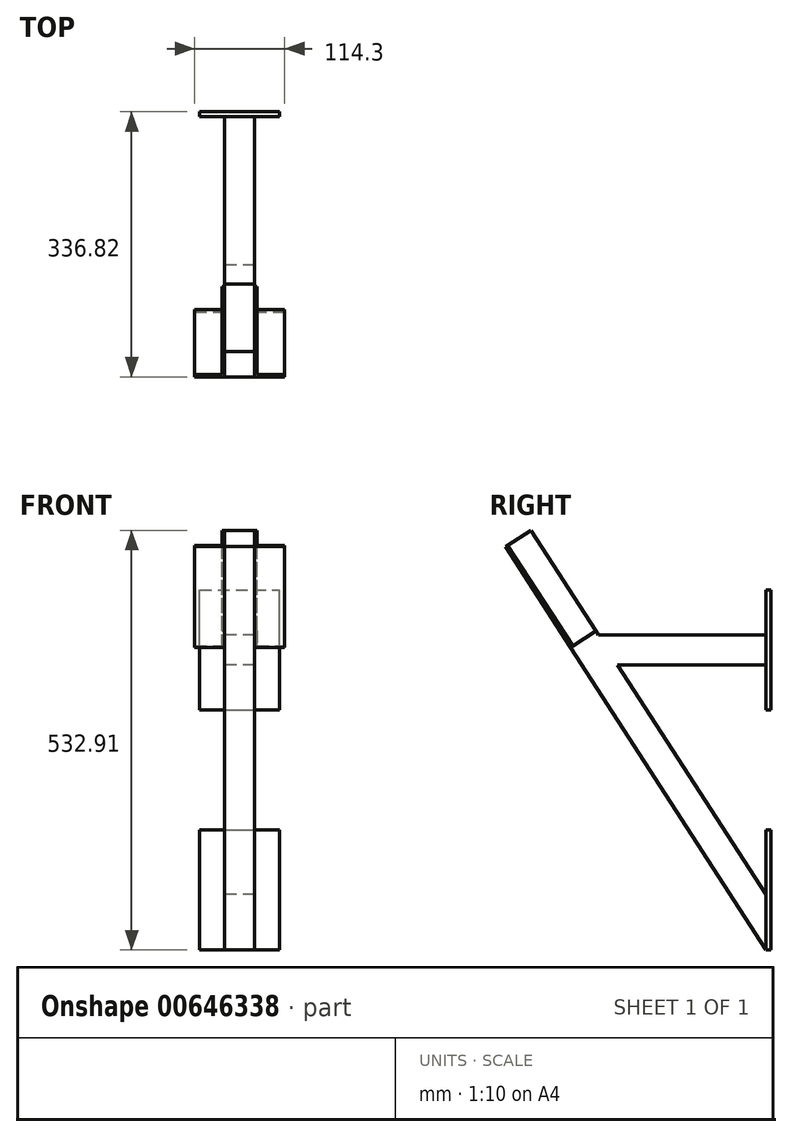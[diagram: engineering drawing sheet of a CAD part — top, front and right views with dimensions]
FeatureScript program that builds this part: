
annotation { "Feature Type Name" : "Feature", "Feature Type Description" : "" }
export const myFeature = defineFeature(function(context is Context, id is Id, definition is map)
    precondition{}
    {
        {
            var Q0;
            Q0=qCreatedBy(makeId("Front.planeOp"),FACE);
            var sketch = newSketch(context, id + "F0", { "sketchPlane" : qUnion([Q0])});
            skLineSegment(sketch, "E0.bottom", {"start": v(-50.8, 0) * mm, "end": v(50.8, 0) * mm});
            skLineSegment(sketch, "E0.top", {"start": v(-50.8, 152.4) * mm, "end": v(50.8, 152.4) * mm});
            skLineSegment(sketch, "E0.left", {"start": v(-50.8, 0) * mm, "end": v(-50.8, 152.4) * mm});
            skLineSegment(sketch, "E0.right", {"start": v(50.8, 0) * mm, "end": v(50.8, 152.4) * mm});
            skLineSegment(sketch, "E1.bottom", {"start": v(-50.8, 304.8) * mm, "end": v(50.8, 304.8) * mm});
            skLineSegment(sketch, "E1.top", {"start": v(-50.8, 457.2) * mm, "end": v(50.8, 457.2) * mm});
            skLineSegment(sketch, "E1.left", {"start": v(-50.8, 304.8) * mm, "end": v(-50.8, 457.2) * mm});
            skLineSegment(sketch, "E1.right", {"start": v(50.8, 304.8) * mm, "end": v(50.8, 457.2) * mm});
            skSolve(sketch);
        }
        {
            var Q0;
            Q0=makeQuery(id+"F0.imprint","IMPRINT",FACE,{"disambiguationData":[TD([[makeQuery(id+"F0.imprint","IMPRINT",EDGE,{"derivedFrom":sQuery(id+"F0.wireOp",EDGE,"E1.bottom")}),1.0]])]});
            var Q1;
            Q1=makeQuery(id+"F0.imprint","IMPRINT",FACE,{"disambiguationData":[TD([[makeQuery(id+"F0.imprint","IMPRINT",EDGE,{"derivedFrom":sQuery(id+"F0.wireOp",EDGE,"E0.bottom")}),1.0]])]});
            extrude(context, id + "F1", {"entities" : qUnion([Q0, Q1]), "oppositeDirection" : true, "depth" : 6.35 * mm, "offsetDistance" : 25.4 * mm});
        }
        {
            var Q0;
            Q0=qCreatedBy(makeId("Right.planeOp"),FACE);
            var sketch = newSketch(context, id + "F2", { "sketchPlane" : qUnion([Q0])});
            skLineSegment(sketch, "E2.0.0", {"start": v(0, 0) * mm, "end": v(0, 152.4) * mm});
            skLineSegment(sketch, "E2.0.1", {"start": v(0, 152.4) * mm, "end": v(6.35, 152.4) * mm});
            skLineSegment(sketch, "E2.0.2", {"start": v(6.35, 152.4) * mm, "end": v(6.35, 0) * mm});
            skLineSegment(sketch, "E2.0.3", {"start": v(6.35, 0) * mm, "end": v(0, 0) * mm});
            skLineSegment(sketch, "E3.0", {"start": v(0, 304.8) * mm, "end": v(0, 457.2) * mm});
            skLineSegment(sketch, "E4.0", {"start": v(6.35, 304.8) * mm, "end": v(0, 304.8) * mm});
            skLineSegment(sketch, "E5", {"start": v(0, 0) * mm, "end": v(-330.47, 512.25) * mm});
            skLineSegment(sketch, "E6.0", {"start": v(0, 70.28) * mm, "end": v(-298.45, 532.9) * mm});
            skLineSegment(sketch, "E7", {"start": v(-330.47, 512.25) * mm, "end": v(-298.45, 532.9) * mm});
            skLineSegment(sketch, "E8", {"start": v(0, 381) * mm, "end": v(-200.45, 381) * mm});
            skLineSegment(sketch, "E9.0", {"start": v(0, 400.05) * mm, "end": v(-212.74, 400.05) * mm});
            skLineSegment(sketch, "E10.0", {"start": v(0, 361.95) * mm, "end": v(-188.16, 361.95) * mm});
            skSolve(sketch);
        }
        {
            var Q0;
            {var subQ5=sQuery(id+"F2.wireOp",EDGE,"E5");Q0=makeQuery(id+"F2.imprint","IMPRINT",FACE,{"disambiguationData":[TD([[makeQuery(id+"F2.imprint","IMPRINT",EDGE,{"derivedFrom":subQ5}),-1.0]])]});}
            var Q1;
            {var subQ0=sQuery(id+"F2.wireOp",EDGE,"E8");Q1=makeQuery(id+"F2.imprint","IMPRINT",FACE,{"disambiguationData":[TD([[makeQuery(id+"F2.imprint","IMPRINT",EDGE,{"derivedFrom":subQ0}),-1.0]])]});}
            var Q2;
            {var subQ0=sQuery(id+"F2.wireOp",EDGE,"E8");Q2=makeQuery(id+"F2.imprint","IMPRINT",FACE,{"disambiguationData":[TD([[makeQuery(id+"F2.imprint","IMPRINT",EDGE,{"derivedFrom":subQ0}),1.0]])]});}
            extrude(context, id + "F3", {"entities" : qUnion([Q0, Q1, Q2]), "endBound" : BoundingType.SYMMETRIC, "depth" : 38.1 * mm, "offsetDistance" : 25.4 * mm});
        }
        {
            var Q0;
            Q0=makeQuery(id+"F3.opExtrude","SWEPT_FACE",FACE,{"disambiguationData":[OSD([sQuery(id+"F2.wireOp",EDGE,"E7")])]});
            var sketch = newSketch(context, id + "F4", { "sketchPlane" : qUnion([Q0])});
            skLineSegment(sketch, "E11.0", {"start": v(-19.05, 0) * mm, "end": v(-19.05, 38.1) * mm});
            skLineSegment(sketch, "E12.0", {"start": v(19.05, 0) * mm, "end": v(19.05, 38.1) * mm});
            skLineSegment(sketch, "E13.0", {"start": v(19.05, 0) * mm, "end": v(-19.05, 0) * mm});
            skLineSegment(sketch, "E14", {"start": v(-57.15, 0) * mm, "end": v(57.15, 0) * mm});
            skLineSegment(sketch, "E15", {"start": v(-57.15, 0) * mm, "end": v(-57.15, 3.18) * mm});
            skLineSegment(sketch, "E16", {"start": v(-57.15, 3.18) * mm, "end": v(-22.22, 3.18) * mm});
            skLineSegment(sketch, "E17", {"start": v(-22.22, 3.18) * mm, "end": v(-22.22, 38.1) * mm});
            skLineSegment(sketch, "E18", {"start": v(-22.22, 38.1) * mm, "end": v(-19.05, 38.1) * mm});
            skLineSegment(sketch, "E19", {"start": v(19.05, 38.1) * mm, "end": v(22.23, 38.1) * mm});
            skLineSegment(sketch, "E20", {"start": v(22.23, 38.1) * mm, "end": v(22.23, 3.17) * mm});
            skLineSegment(sketch, "E21", {"start": v(22.23, 3.17) * mm, "end": v(57.15, 3.18) * mm});
            skLineSegment(sketch, "E22", {"start": v(57.15, 3.18) * mm, "end": v(57.15, 0) * mm});
            skSolve(sketch);
        }
        {
            var Q0;
            {var subQ1=sQuery(id+"F4.wireOp",EDGE,"E11.0");Q0=makeQuery(id+"F4.imprint","IMPRINT",FACE,{"disambiguationData":[TD([[makeQuery(id+"F4.imprint","IMPRINT",EDGE,{"derivedFrom":subQ1}),1.0]])]});}
            var Q1;
            {var subQ1=sQuery(id+"F4.wireOp",EDGE,"E12.0");Q1=makeQuery(id+"F4.imprint","IMPRINT",FACE,{"disambiguationData":[TD([[makeQuery(id+"F4.imprint","IMPRINT",EDGE,{"derivedFrom":subQ1}),-1.0]])]});}
            extrude(context, id + "F5", {"entities" : qUnion([Q0, Q1]), "oppositeDirection" : true, "depth" : 152.4 * mm, "offsetDistance" : 25.4 * mm});
        }
    });
